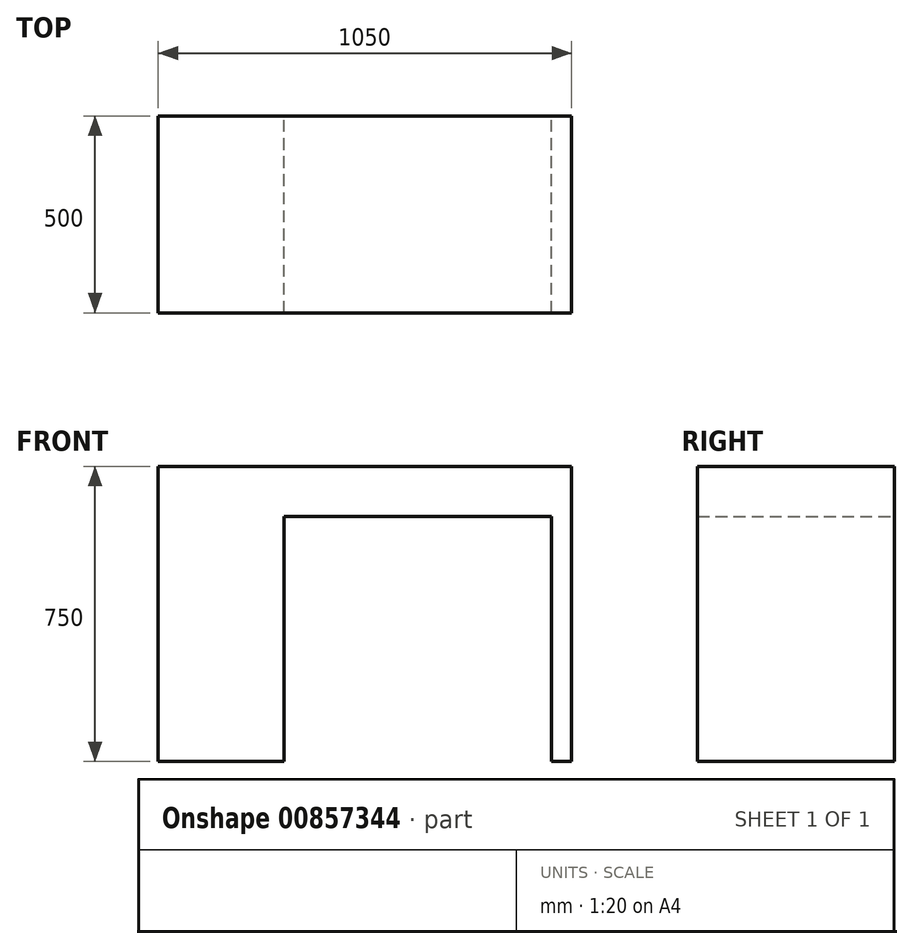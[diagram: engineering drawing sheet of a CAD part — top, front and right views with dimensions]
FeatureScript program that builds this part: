
annotation { "Feature Type Name" : "Feature", "Feature Type Description" : "" }
export const myFeature = defineFeature(function(context is Context, id is Id, definition is map)
    precondition{}
    {
        {
            var Q0;
            Q0=qCreatedBy(makeId("Front.planeOp"),FACE);
            var sketch = newSketch(context, id + "F0", { "sketchPlane" : qUnion([Q0])});
            skLineSegment(sketch, "E0.bottom", {"start": v(0, 0) * mm, "end": v(320, 0) * mm});
            skLineSegment(sketch, "E0.top", {"start": v(0, 750) * mm, "end": v(1050, 750) * mm});
            skLineSegment(sketch, "E0.left", {"start": v(0, 0) * mm, "end": v(0, 750) * mm});
            skLineSegment(sketch, "E0.right", {"start": v(1050, 0) * mm, "end": v(1050, 750) * mm});
            skLineSegment(sketch, "E1.top", {"start": v(320, 623) * mm, "end": v(999.2, 623) * mm});
            skLineSegment(sketch, "E1.left", {"start": v(320, 0) * mm, "end": v(320, 623) * mm});
            skLineSegment(sketch, "E1.right", {"start": v(999.2, 0) * mm, "end": v(999.2, 623) * mm});
            skLineSegment(sketch, "E2.trimOffspring", {"start": v(999.2, 0) * mm, "end": v(1050, 0) * mm});
            skSolve(sketch);
        }
        {
            var Q0;
            Q0 = qSketchRegion(id + "F0", true);
            extrude(context, id + "F1", {"entities" : qUnion([Q0]), "depth" : 500 * mm, "offsetDistance" : 25.4 * mm});
        }
    });
